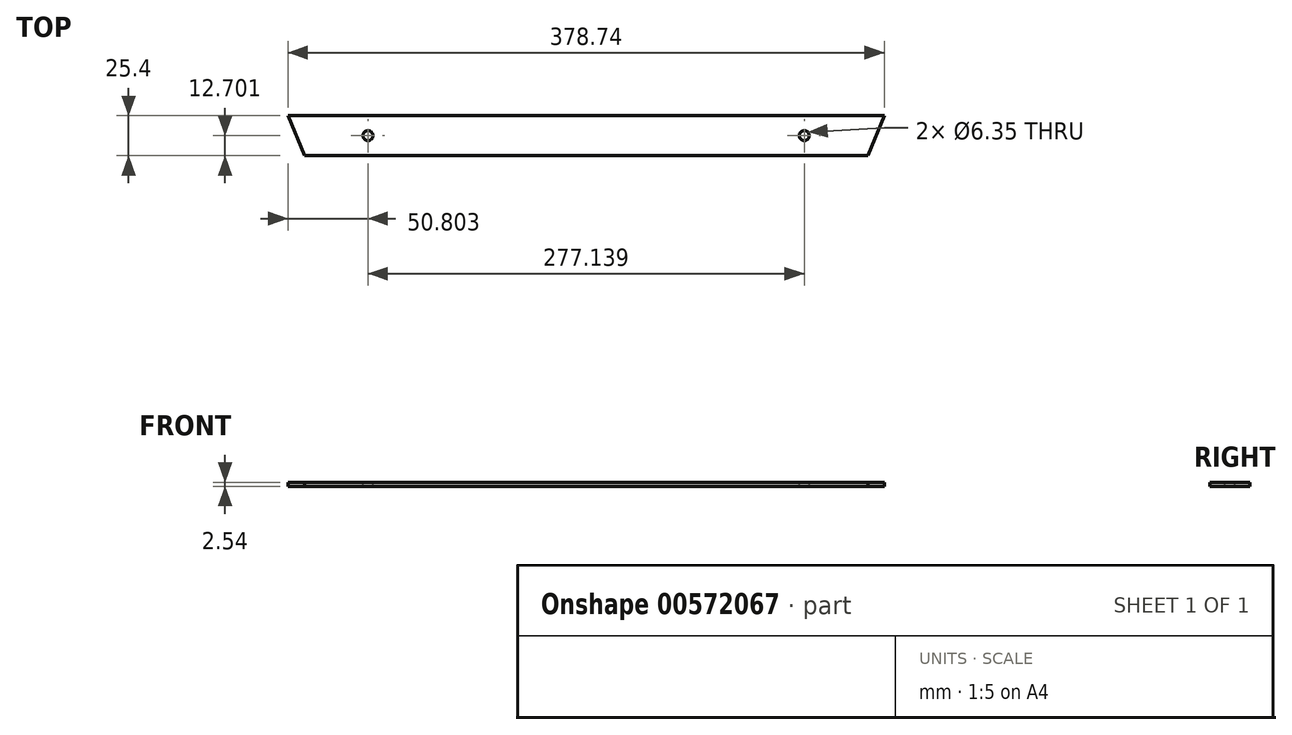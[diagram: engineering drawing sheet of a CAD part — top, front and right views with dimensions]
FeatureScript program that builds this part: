
annotation { "Feature Type Name" : "Feature", "Feature Type Description" : "" }
export const myFeature = defineFeature(function(context is Context, id is Id, definition is map)
    precondition{}
    {
        {
            var Q0;
            Q0=qCreatedBy(makeId("Top.planeOp"),FACE);
            var sketch = newSketch(context, id + "F0", { "sketchPlane" : qUnion([Q0])});
            skLineSegment(sketch, "E0.bottom", {"start": v(-147.37, -21.76) * mm, "end": v(231.37, -21.76) * mm});
            skLineSegment(sketch, "E0.top", {"start": v(-147.37, -47.16) * mm, "end": v(231.37, -47.16) * mm});
            skLineSegment(sketch, "E0.left", {"start": v(-147.37, -21.76) * mm, "end": v(-147.37, -47.16) * mm});
            skLineSegment(sketch, "E0.right", {"start": v(231.37, -21.76) * mm, "end": v(231.37, -47.16) * mm});
            skSolve(sketch);
        }
        {
            var Q0;
            Q0 = qSketchRegion(id + "F0", true);
            extrude(context, id + "F1", {"entities" : qUnion([Q0]), "depth" : 2.54 * mm, "offsetDistance" : 25.4 * mm});
        }
        {
            var Q0;
            Q0=makeQuery(id+"F1.opExtrude","CAP_FACE",FACE,{"disambiguationData":[OSD([sQuery(id+"F0.wireOp",EDGE,"E0.bottom"),sQuery(id+"F0.wireOp",EDGE,"E0.top"),sQuery(id+"F0.wireOp",EDGE,"E0.left"),sQuery(id+"F0.wireOp",EDGE,"E0.right")])],"isStart":false});
            var sketch = newSketch(context, id + "F2", { "sketchPlane" : qUnion([Q0])});
            skLineSegment(sketch, "E1", {"start": v(-147.37, -21.76) * mm, "end": v(-136.85, -47.16) * mm});
            skLineSegment(sketch, "E2", {"start": v(231.37, -21.76) * mm, "end": v(220.85, -47.16) * mm});
            skLineSegment(sketch, "E3", {"start": v(220.85, -47.16) * mm, "end": v(231.37, -47.16) * mm});
            skLineSegment(sketch, "E4", {"start": v(-136.85, -47.16) * mm, "end": v(-147.37, -47.16) * mm});
            skSolve(sketch);
        }
        {
            var Q0;
            Q0=makeQuery(id+"F2.imprint","IMPRINT",FACE,{"disambiguationData":[TD([[makeQuery(id+"F2.imprint","IMPRINT",EDGE,{"derivedFrom":sQuery(id+"F2.wireOp",EDGE,"E1")}),-1.0]])]});
            var Q1;
            Q1=makeQuery(id+"F2.imprint","IMPRINT",FACE,{"disambiguationData":[TD([[makeQuery(id+"F2.imprint","IMPRINT",EDGE,{"derivedFrom":sQuery(id+"F2.wireOp",EDGE,"E2")}),1.0]])]});
            extrude(context, id + "F3", {"entities" : qUnion([Q0, Q1]), "operationType" : NewBodyOperationType.REMOVE, "endBound" : BoundingType.THROUGH_ALL, "oppositeDirection" : true, "depth" : 25.4 * mm, "offsetDistance" : 25.4 * mm});
        }
        {
            var Q0;
            Q0=makeQuery(id+"F1.opExtrude","CAP_FACE",FACE,{"disambiguationData":[OSD([sQuery(id+"F0.wireOp",EDGE,"E0.bottom"),sQuery(id+"F0.wireOp",EDGE,"E0.top"),sQuery(id+"F0.wireOp",EDGE,"E0.left"),sQuery(id+"F0.wireOp",EDGE,"E0.right")])],"isStart":false});
            var sketch = newSketch(context, id + "F4", { "sketchPlane" : qUnion([Q0])});
            skCircle(sketch, "E5", {"center": v(-96.57, -34.46) * mm, "radius": 3.18 * mm});
            skCircle(sketch, "E6", {"center": v(180.57, -34.46) * mm, "radius": 3.17 * mm});
            skLineSegment(sketch, "E7", {"start": v(-99.31, -32.86) * mm, "end": v(-96.57, -34.46) * mm});
            skLineSegment(sketch, "E8", {"start": v(180.57, -34.46) * mm, "end": v(177.4, -34.46) * mm});
            skSolve(sketch);
        }
        {
            var Q0;
            Q0 = qSketchRegion(id + "F4", true);
            extrude(context, id + "F5", {"entities" : qUnion([Q0]), "operationType" : NewBodyOperationType.REMOVE, "endBound" : BoundingType.THROUGH_ALL, "oppositeDirection" : true, "depth" : 25.4 * mm, "offsetDistance" : 25.4 * mm});
        }
    });
